# Revit family: Maxi Line System Rolling Gondola
name_source: partatom
category: Generic Models
revit_build: Autodesk Revit Architecture 2012 (Build: 20110309_2315(x64)
units: mm (PartAtom-declared; Revit-internal decimal feet)

## types (1)
- Maxi Line System Rolling Gondola
    Caster Group 1 on/off = Yes
    Caster Group 2 on/off = No
    Caster Group 3 on/off = No
    Caster Material = Default Madix
    Center Panel 1 on/off = Yes
    Center Panel 2 on/off = No
    Center Panel 3 on/off = No
    Center Panel Height = 6' - 1"
    Center Panel Width = 4' - 0"
    End Panel 2 on/off = No
    End Panel 3 on/off = Yes
    End Panel 4 on/off = No
    End Panel 5 on/off = No
    End Panel Height = 6' - 0"
    End Panel Width = 3' - 0"
    Frame Material = Default Madix
    Model = Maxi Line System Rolling Gondola
    Panel Material = Default Madix
    URL = http://www.madixinc.com

## geometry (parser evidence)
native form markers: Blend x6, Extrusion x1, Sweep x15
no freeform markers — native parametric forms only
